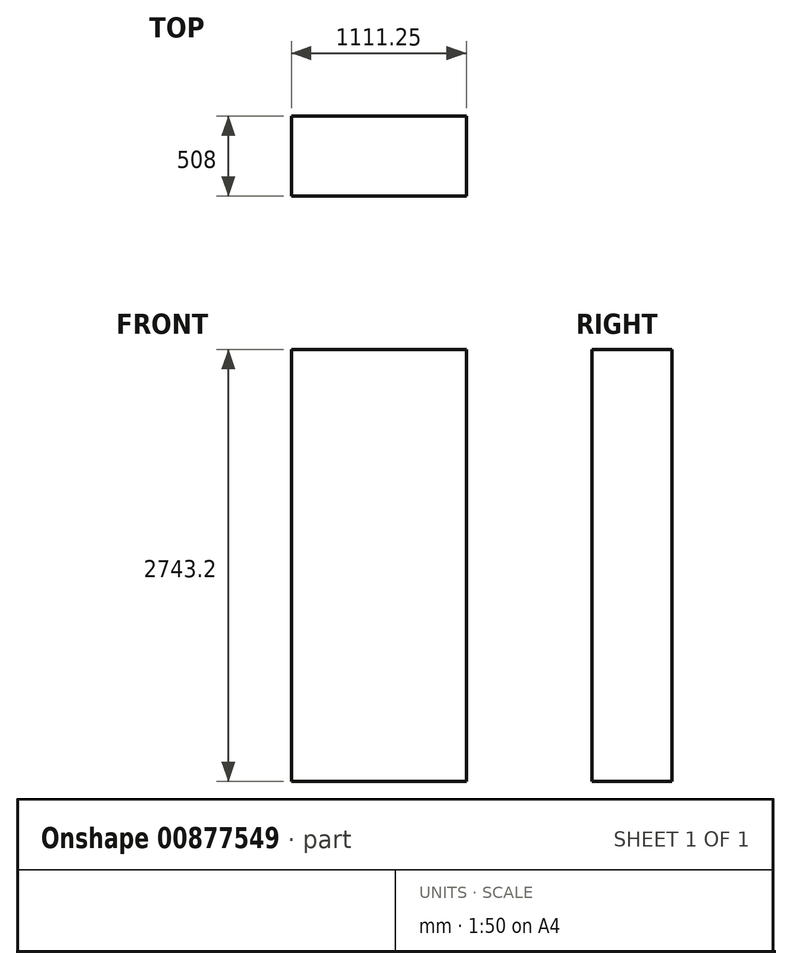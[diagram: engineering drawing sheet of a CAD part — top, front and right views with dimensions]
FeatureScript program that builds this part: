
annotation { "Feature Type Name" : "Feature", "Feature Type Description" : "" }
export const myFeature = defineFeature(function(context is Context, id is Id, definition is map)
    precondition{}
    {
        {
            var Q0;
            Q0=qCreatedBy(makeId("Top.planeOp"),FACE);
            var sketch = newSketch(context, id + "F0", { "sketchPlane" : qUnion([Q0])});
            skLineSegment(sketch, "E0.top", {"start": v(0, 508) * mm, "end": v(1111.25, 508) * mm});
            skLineSegment(sketch, "E0.left", {"start": v(0, 0) * mm, "end": v(0, 508) * mm});
            skLineSegment(sketch, "E0.right", {"start": v(1111.25, 0) * mm, "end": v(1111.25, 508) * mm});
            skSolve(sketch);
        }
        {
            var Q0;
            Q0 = qSketchRegion(id + "F0", true);
            var Q1;
            Q1=sQuery(id+"F0.wireOp",EDGE,"E0.left");
            var Q2;
            Q2=sQuery(id+"F0.wireOp",EDGE,"E0.top");
            var Q3;
            Q3=sQuery(id+"F0.wireOp",EDGE,"E0.right");
            extrude(context, id + "F1", {"entities" : qUnion([Q0]), "bodyType" : ToolBodyType.SURFACE, "surfaceEntities" : qUnion([Q1, Q2, Q3]), "depth" : 2743.2 * mm, "offsetDistance" : 25.4 * mm});
        }
        {
            var Q0;
            Q0=qCreatedBy(makeId("Front.planeOp"),FACE);
            var sketch = newSketch(context, id + "F2", { "sketchPlane" : qUnion([Q0])});
            skLineSegment(sketch, "E1", {"start": v(0, 0) * mm, "end": v(1111.25, 0) * mm});
            skSolve(sketch);
        }
        {
            var Q0;
            Q0 = qSketchRegion(id + "F2", true);
            var Q1;
            Q1=sQuery(id+"F2.wireOp",EDGE,"E1");
            var Q2;
            Q2=makeQuery(id+"F1.opExtrude","SWEPT_FACE",FACE,{"disambiguationData":[OSD([sQuery(id+"F0.wireOp",EDGE,"E0.top")])]});
            extrude(context, id + "F3", {"entities" : qUnion([Q0]), "bodyType" : ToolBodyType.SURFACE, "surfaceEntities" : qUnion([Q1]), "endBound" : BoundingType.UP_TO_SURFACE, "oppositeDirection" : true, "depth" : 25.4 * mm, "endBoundEntityFace" : qUnion([Q2]), "offsetDistance" : 25.4 * mm});
        }
        {
            var Q0;
            Q0=qCreatedBy(makeId("Front.planeOp"),FACE);
            var sketch = newSketch(context, id + "F4", { "sketchPlane" : qUnion([Q0])});
            skLineSegment(sketch, "E2", {"start": v(1111.25, 2743.2) * mm, "end": v(0, 2743.2) * mm});
            skSolve(sketch);
        }
        {
            var Q0;
            Q0 = qSketchRegion(id + "F4", true);
            var Q1;
            Q1=sQuery(id+"F4.wireOp",EDGE,"E2");
            var Q2;
            Q2=makeQuery(id+"F1.opExtrude","SWEPT_FACE",FACE,{"disambiguationData":[OSD([sQuery(id+"F0.wireOp",EDGE,"E0.top")])]});
            extrude(context, id + "F5", {"entities" : qUnion([Q0]), "bodyType" : ToolBodyType.SURFACE, "surfaceEntities" : qUnion([Q1]), "endBound" : BoundingType.UP_TO_SURFACE, "oppositeDirection" : true, "depth" : 25.4 * mm, "endBoundEntityFace" : qUnion([Q2]), "offsetDistance" : 25.4 * mm});
        }
        {
            var Q0;
            Q0=makeQuery(id+"F1.opExtrude","SWEPT_FACE",FACE,{"disambiguationData":[OSD([sQuery(id+"F0.wireOp",EDGE,"E0.top")])]});
            var sketch = newSketch(context, id + "F6", { "sketchPlane" : qUnion([Q0])});
            skLineSegment(sketch, "E3", {"start": v(0, 533.4) * mm, "end": v(1111.25, 533.4) * mm});
            skLineSegment(sketch, "E4", {"start": v(304.8, 533.4) * mm, "end": v(304.8, 0) * mm});
            skLineSegment(sketch, "E5", {"start": v(806.45, 533.4) * mm, "end": v(806.45, 0) * mm});
            skLineSegment(sketch, "E6", {"start": v(304.8, 355.6) * mm, "end": v(911.23, 355.6) * mm});
            skLineSegment(sketch, "E7", {"start": v(304.8, 165.1) * mm, "end": v(911.23, 165.1) * mm});
            skLineSegment(sketch, "E8", {"start": v(1111.25, 552.45) * mm, "end": v(0, 552.45) * mm});
            skLineSegment(sketch, "E9", {"start": v(228.6, 552.45) * mm, "end": v(228.6, 2743.2) * mm});
            skLineSegment(sketch, "E10", {"start": v(806.45, 552.45) * mm, "end": v(806.45, 2743.2) * mm});
            skLineSegment(sketch, "E11", {"start": v(1111.25, 965.2) * mm, "end": v(390.53, 965.2) * mm});
            skLineSegment(sketch, "E12", {"start": v(1111.25, 1244.6) * mm, "end": v(704.85, 1244.6) * mm});
            skLineSegment(sketch, "E13", {"start": v(1111.25, 1828.8) * mm, "end": v(123.83, 1828.8) * mm});
            skLineSegment(sketch, "E14", {"start": v(1111.25, 2133.6) * mm, "end": v(0, 2133.6) * mm});
            skLineSegment(sketch, "E15", {"start": v(0, 1625.6) * mm, "end": v(330.2, 1625.6) * mm});
            skLineSegment(sketch, "E16", {"start": v(123.82, 2311.4) * mm, "end": v(911.23, 2311.4) * mm});
            skLineSegment(sketch, "E17", {"start": v(0, 2489.2) * mm, "end": v(330.2, 2489.2) * mm});
            skLineSegment(sketch, "E18", {"start": v(555.62, 0) * mm, "end": v(555.62, 2743.2) * mm, "construction": true});
            skSolve(sketch);
        }
    });
